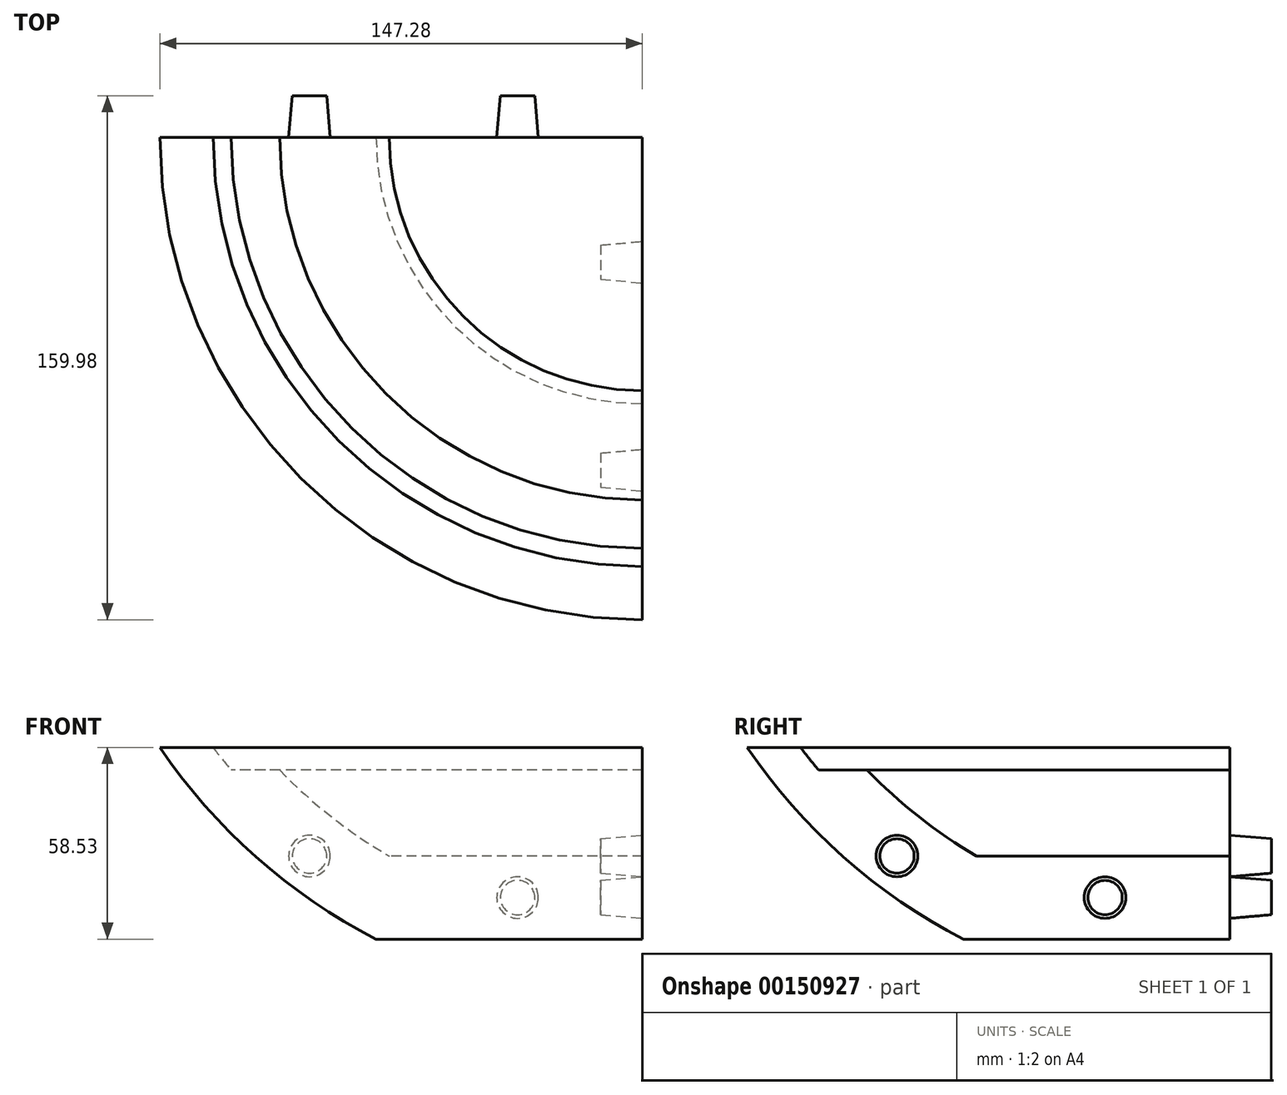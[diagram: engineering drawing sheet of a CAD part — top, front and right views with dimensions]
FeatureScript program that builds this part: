
annotation { "Feature Type Name" : "Feature", "Feature Type Description" : "" }
export const myFeature = defineFeature(function(context is Context, id is Id, definition is map)
    precondition{}
    {
        {
            var Q0;
            Q0=qCreatedBy(makeId("Front.planeOp"),FACE);
            var sketch = newSketch(context, id + "F0", { "sketchPlane" : qUnion([Q0])});
            skLineSegment(sketch, "E0", {"start": v(0, -158.13) * mm, "end": v(-81.28, -158.13) * mm});
            skArc(sketch, "E1", {"start": v(-147.28, -99.6) * mm, "mid": v(-117.97, -133.03) * mm, "end": v(-81.28, -158.13) * mm});
            skLineSegment(sketch, "E2", {"start": v(0, -158.13) * mm, "end": v(0, -132.73) * mm});
            skLineSegment(sketch, "E3", {"start": v(0, -132.73) * mm, "end": v(-77.33, -132.73) * mm});
            skArc(sketch, "E4", {"start": v(-110.71, -106.5) * mm, "mid": v(-94.93, -120.77) * mm, "end": v(-77.33, -132.73) * mm});
            skArc(sketch, "E5", {"start": v(-131.04, -99.6) * mm, "mid": v(-128.32, -103.09) * mm, "end": v(-125.5, -106.5) * mm});
            skLineSegment(sketch, "E6", {"start": v(-147.28, -99.6) * mm, "end": v(-131.04, -99.6) * mm});
            skLineSegment(sketch, "E7", {"start": v(-125.46, -106.5) * mm, "end": v(-125.5, -106.5) * mm});
            skLineSegment(sketch, "E8", {"start": v(-110.71, -106.5) * mm, "end": v(-125.46, -106.5) * mm});
            skSolve(sketch);
        }
        {
            var Q0;
            Q0=makeQuery(id+"F0.imprint","IMPRINT",FACE,{"disambiguationData":[TD([[makeQuery(id+"F0.imprint","IMPRINT",EDGE,{"derivedFrom":sQuery(id+"F0.wireOp",EDGE,"E0")}),-1.0]])]});
            var Q1;
            Q1=sQuery(id+"F0.wireOp",EDGE,"E2");
            revolve(context, id + "F1", {"entities" : qUnion([Q0]), "axis" : qUnion([Q1]), "revolveType" : RevolveType.ONE_DIRECTION, "angle" : 90 * degree});
        }
        {
            var Q0;
            Q0=makeQuery(id+"F1.opRevolve","SWEPT_FACE",FACE,{"disambiguationData":[OSD([sQuery(id+"F0.wireOp",EDGE,"61ceb981-69e5-4026-b42d-312605be9a4c1")])]});
            var Q1;
            Q1=makeQuery(id+"F1.opRevolve","CAP_FACE",FACE,{"disambiguationData":[OSD([sQuery(id+"F0.wireOp",EDGE,"E0"),sQuery(id+"F0.wireOp",EDGE,"E2"),sQuery(id+"F0.wireOp",EDGE,"61ceb981-69e5-4026-b42d-312605be9a4c1"),sQuery(id+"F0.wireOp",EDGE,"E3")])],"isStart":false});
            var Q2;
            Q2=makeQuery(id+"F1.opRevolve","SWEPT_FACE",FACE,{"disambiguationData":[OSD([sQuery(id+"F0.wireOp",EDGE,"E3")])]});
            shell(context, id + "F2", {"entities" : qUnion([Q0, Q1, Q2]), "thickness" : 25.4 * mm});
        }
        {
            var Q0;
            Q0=makeQuery(id+"F0.imprint","IMPRINT",FACE,{"disambiguationData":[TD([[makeQuery(id+"F0.imprint","IMPRINT",EDGE,{"derivedFrom":sQuery(id+"F0.wireOp",EDGE,"E0")}),-1.0]])]});
            var sketch = newSketch(context, id + "F3", { "sketchPlane" : qUnion([Q0])});
            skCircle(sketch, "E9", {"center": v(-101.6, -132.73) * mm, "radius": 6.35 * mm});
            skCircle(sketch, "E10", {"center": v(-38.1, -145.43) * mm, "radius": 6.35 * mm});
            skSolve(sketch);
        }
        {
            var Q0;
            Q0 = qSketchRegion(id + "F3", true);
            extrude(context, id + "F4", {"entities" : qUnion([Q0]), "operationType" : NewBodyOperationType.ADD, "oppositeDirection" : true, "depth" : 12.7 * mm, "hasDraft" : true, "draftAngle" : 5 * degree, "draftPullDirection" : true});
        }
        {
            var Q0;
            Q0=makeQuery(id+"F1.opRevolve","CAP_FACE",FACE,{"disambiguationData":[OSD([sQuery(id+"F0.wireOp",EDGE,"E0"),sQuery(id+"F0.wireOp",EDGE,"E1"),sQuery(id+"F0.wireOp",EDGE,"E2"),sQuery(id+"F0.wireOp",EDGE,"KVrDBEFT-p1Pk-LbOc-m4sr-b6uQapF1O2EA")])],"isStart":false});
            var sketch = newSketch(context, id + "F5", { "sketchPlane" : qUnion([Q0])});
            skCircle(sketch, "E11", {"center": v(-101.6, -132.73) * mm, "radius": 6.35 * mm});
            skCircle(sketch, "E12", {"center": v(-38.1, -145.43) * mm, "radius": 6.35 * mm});
            skSolve(sketch);
        }
        {
            var Q0;
            Q0=makeQuery(id+"F5.imprint","IMPRINT",FACE,{"disambiguationData":[TD([[makeQuery(id+"F5.imprint","IMPRINT",EDGE,{"derivedFrom":sQuery(id+"F5.wireOp",EDGE,"E11")}),1.0]])]});
            var Q1;
            Q1=makeQuery(id+"F5.imprint","IMPRINT",FACE,{"disambiguationData":[TD([[makeQuery(id+"F5.imprint","IMPRINT",EDGE,{"derivedFrom":sQuery(id+"F5.wireOp",EDGE,"E12")}),1.0]])]});
            var Q2;
            Q2=sQuery(id+"F5.wireOp",EDGE,"E11");
            var Q3;
            Q3=sQuery(id+"F5.wireOp",EDGE,"E12");
            extrude(context, id + "F6", {"entities" : qUnion([Q0, Q1]), "operationType" : NewBodyOperationType.REMOVE, "surfaceEntities" : qUnion([Q2, Q3]), "oppositeDirection" : true, "depth" : 12.7 * mm, "hasDraft" : true, "draftAngle" : 5 * degree, "draftPullDirection" : true});
        }
    });
